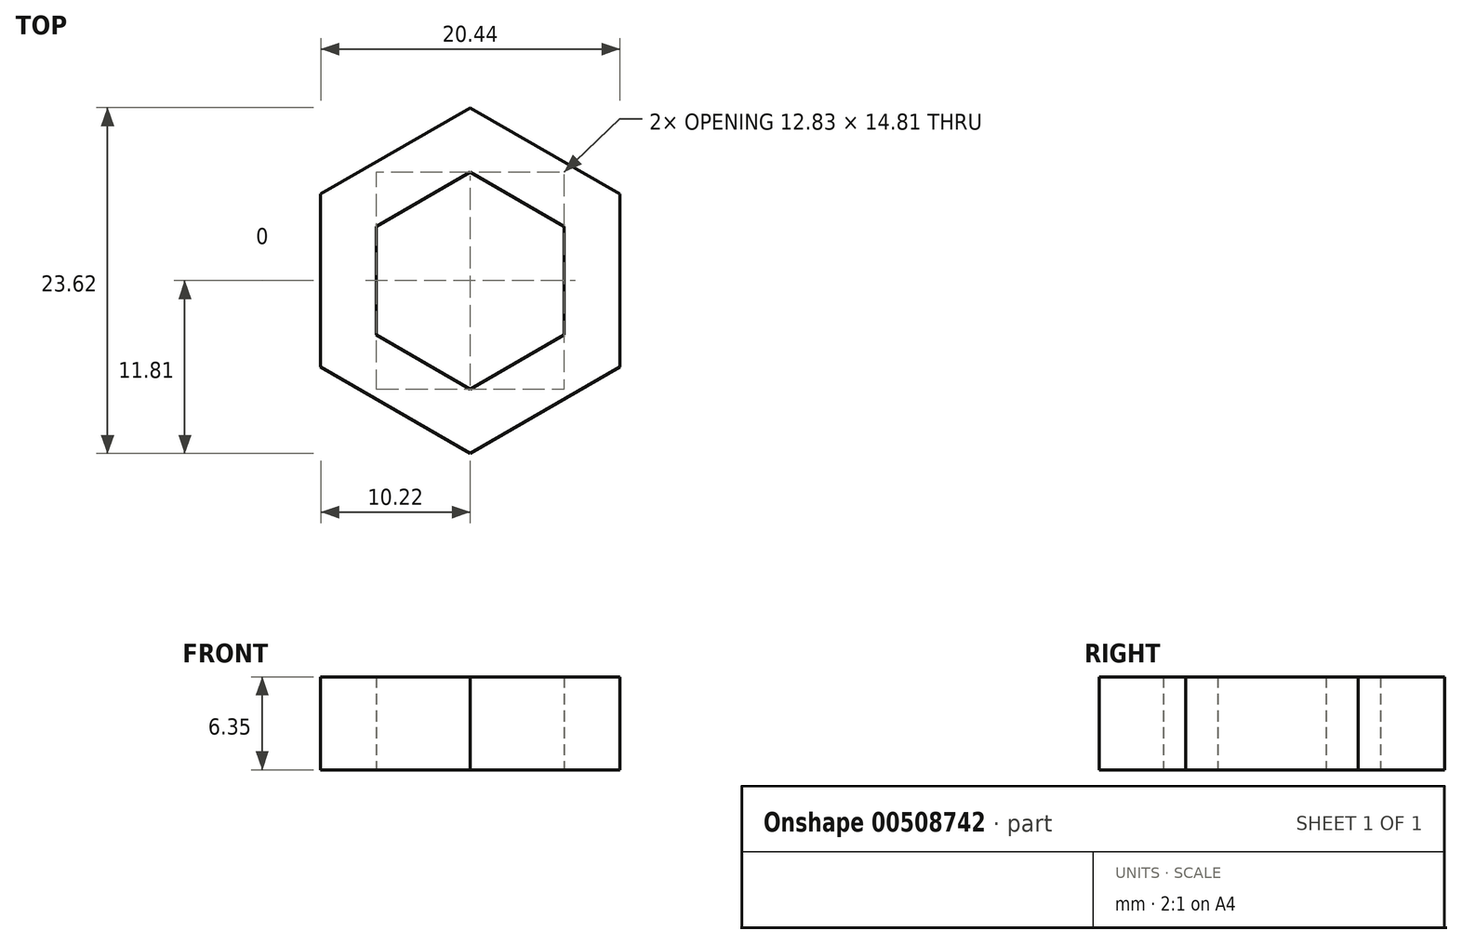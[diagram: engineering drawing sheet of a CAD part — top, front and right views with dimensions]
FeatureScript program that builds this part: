
annotation { "Feature Type Name" : "Feature", "Feature Type Description" : "" }
export const myFeature = defineFeature(function(context is Context, id is Id, definition is map)
    precondition{}
    {
        {
            var Q0;
            Q0=qCreatedBy(makeId("Top.planeOp"),FACE);
            var sketch = newSketch(context, id + "F0", { "sketchPlane" : qUnion([Q0])});
            skCircle(sketch, "E0.cCircle", {"center": v(0, 0) * mm, "radius": 6.41 * mm, "construction": true});
            skLineSegment(sketch, "E0.0", {"start": v(6.41, 3.7) * mm, "end": v(6.41, -3.7) * mm});
            skLineSegment(sketch, "E0.1", {"start": v(6.41, -3.7) * mm, "end": v(0, -7.4) * mm});
            skLineSegment(sketch, "E0.2", {"start": v(0, -7.4) * mm, "end": v(-6.41, -3.7) * mm});
            skLineSegment(sketch, "E0.3", {"start": v(-6.41, -3.7) * mm, "end": v(-6.41, 3.7) * mm});
            skLineSegment(sketch, "E0.4", {"start": v(-6.41, 3.7) * mm, "end": v(0, 7.4) * mm});
            skLineSegment(sketch, "E0.5", {"start": v(0, 7.4) * mm, "end": v(6.41, 3.7) * mm});
            skPoint(sketch, "E0.0.midPoint", {"position": v(6.41, 0) * mm});
            skLineSegment(sketch, "E1.0", {"start": v(-10.22, 5.9) * mm, "end": v(0, 11.8) * mm});
            skLineSegment(sketch, "E1.1", {"start": v(10.22, 5.9) * mm, "end": v(10.22, -5.9) * mm});
            skLineSegment(sketch, "E1.2", {"start": v(10.22, -5.9) * mm, "end": v(0, -11.8) * mm});
            skLineSegment(sketch, "E1.3", {"start": v(0, 11.8) * mm, "end": v(10.22, 5.9) * mm});
            skLineSegment(sketch, "E1.4", {"start": v(0, -11.8) * mm, "end": v(-10.22, -5.9) * mm});
            skLineSegment(sketch, "E1.5", {"start": v(-10.22, -5.9) * mm, "end": v(-10.22, 5.9) * mm});
            skSolve(sketch);
        }
        {
            var Q0;
            Q0=makeQuery(id+"F0.imprint","IMPRINT",FACE,{"disambiguationData":[TD([[makeQuery(id+"F0.imprint","IMPRINT",EDGE,{"derivedFrom":sQuery(id+"F0.wireOp",EDGE,"E0.0")}),1.0]])]});
            extrude(context, id + "F1", {"entities" : qUnion([Q0]), "depth" : 6.35 * mm});
        }
    });
